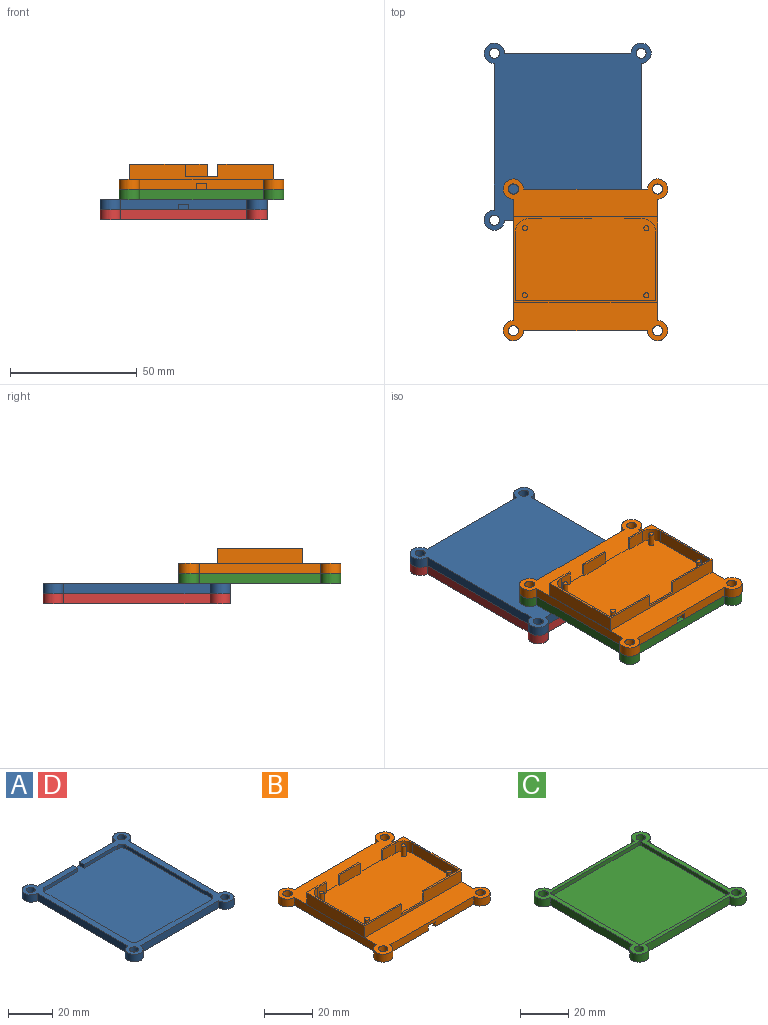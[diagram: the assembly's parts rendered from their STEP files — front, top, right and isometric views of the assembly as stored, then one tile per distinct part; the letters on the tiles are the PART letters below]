
ASSEMBLY  parts=4 mates=7
PART A: 26 faces, bbox 66x74x4 mm
  f0: plane 74x66mm, normal (0,0,1), area 804.3mm2, adj f1,f2,f3,f4,f5,f6,f7,f8
  f1: cylinder r=4mm len=8mm, axis (0,0,-1), area 75.4mm2, adj f0,f2,f8,f9
  f2: plane 50x4mm, normal (0,1,0), area 192mm2, adj f0,f1,f3,f9,f10,f11,f12
  f3: cylinder r=4mm len=8mm, axis (0,0,-1), area 75.4mm2, adj f0,f2,f4,f9
  f4: plane 58x4mm, normal (-1,0,0), area 232mm2, adj f0,f3,f5,f9
  f5: cylinder r=4mm len=8mm, axis (0,0,-1), area 75.4mm2, adj f0,f4,f6,f9
  f6: plane 50x4mm, normal (0,-1,0), area 200mm2, adj f0,f5,f7,f9
  f7: cylinder r=4mm len=8mm, axis (0,0,-1), area 75.4mm2, adj f0,f6,f8,f9
  f8: plane 58x4mm, normal (1,0,0), area 232mm2, adj f0,f1,f7,f9
  f9: plane 74x66mm, normal (0,0,-1), area 3928.5mm2, adj f1,f2,f3,f4,f5,f6,f7,f8
  f10: plane 3x2mm, normal (1,0,0), area 6mm2, adj f0,f2,f12,f15
  f11: plane 3x2mm, normal (-1,0,0), area 6mm2, adj f0,f2,f12,f13
  f12: plane 63x52mm, normal (0,0,1), area 3124.3mm2, adj f2,f10,f11,f13,f14,f15,f16,f17
  f13: plane 21x2mm, normal (0,-1,0), area 42mm2, adj f0,f11,f12,f22
  f14: plane 54x2mm, normal (-1,0,0), area 108mm2, adj f0,f12,f22,f25
  f15: plane 21x2mm, normal (0,-1,0), area 42mm2, adj f0,f10,f12,f23
  f16: plane 54x2mm, normal (1,0,0), area 108mm2, adj f0,f12,f23,f24
  f17: plane 46x2mm, normal (0,1,0), area 92mm2, adj f0,f12,f24,f25
  f18: cylinder r=2mm len=4mm, axis (0,0,-1), area 50.3mm2, adj f0,f9
  f19: cylinder r=2mm len=4mm, axis (0,0,-1), area 50.3mm2, adj f0,f9
  f20: cylinder r=2mm len=4mm, axis (0,0,-1), area 50.3mm2, adj f0,f9
  f21: cylinder r=2mm len=4mm, axis (0,0,-1), area 50.3mm2, adj f0,f9
  f22: cylinder r=3mm len=3mm, axis (0,0,1), area 9.4mm2, adj f0,f12,f13,f14
  f23: cylinder r=3mm len=3mm, axis (0,0,-1), area 9.4mm2, adj f0,f12,f15,f16
  f24: cylinder r=3mm len=3mm, axis (0,0,1), area 9.4mm2, adj f0,f12,f16,f17
  f25: cylinder r=3mm len=3mm, axis (0,0,-1), area 9.4mm2, adj f0,f12,f14,f17
PART B: 57 faces, bbox 65x64x10 mm
  f0: plane 65x64mm, normal (0,0,-1), area 478.4mm2, adj f27,f28,f29,f30,f31,f32,f33,f34
  f1: plane 33.9x22mm, normal (0,0,1), area 55.9mm2, adj f2,f7,f9,f10,f11,f13,f25,f36
  f2: plane 55.4x5.25mm, normal (0,1,0), area 226.3mm2, adj f1,f4,f12,f13,f14,f36,f37,f38
  f3: plane 12.25x0.75mm, normal (0,0,1), area 9.2mm2, adj f5,f7,f24,f26
  f4: plane 33.9x22mm, normal (0,0,1), area 54.4mm2, adj f2,f6,f7,f8,f9,f12,f23,f37
  f5: plane 12.25x5.25mm, normal (0,-1,0), area 64.3mm2, adj f3,f14,f24,f26
  f6: plane 5.25x5.2mm, normal (0,-1,0), area 27.3mm2, adj f4,f14,f23,f53
  f7: plane 56.9x6mm, normal (0,1,0), area 232.5mm2, adj f1,f3,f4,f8,f10,f14,f23,f24
  f8: plane 33.9x6mm, normal (-1,0,0), area 203.4mm2, adj f4,f7,f9,f35
  f9: plane 56.9x6mm, normal (0,-1,0), area 276.9mm2, adj f1,f4,f8,f10,f35,f36,f37,f38
  f10: plane 33.9x6mm, normal (1,0,0), area 203.4mm2, adj f1,f7,f9,f35
  f11: plane 7.2x5.25mm, normal (0,-1,0), area 37.8mm2, adj f1,f14,f25,f52
  f12: plane 27.4x5.25mm, normal (1,0,0), area 143.8mm2, adj f2,f4,f14,f53
  f13: plane 27.4x5.25mm, normal (-1,0,0), area 143.8mm2, adj f1,f2,f14,f52
  f14: plane 55.4x33.15mm, normal (0,0,1), area 1787.2mm2, adj f2,f5,f6,f7,f11,f12,f13,f15
  f15: cylinder r=1mm len=5.25mm, axis (0,0,-1), area 33mm2, adj f14,f16
  f16: plane 2x2mm, normal (0,0,1), area 3.1mm2, adj f15
  f17: cylinder r=1mm len=5.25mm, axis (0,0,-1), area 33mm2, adj f14,f18
  f18: plane 2x2mm, normal (0,0,1), area 3.1mm2, adj f17
  f19: cylinder r=1mm len=5.25mm, axis (0,0,-1), area 33mm2, adj f14,f20
  f20: plane 2x2mm, normal (0,0,1), area 3.1mm2, adj f19
  f21: cylinder r=1mm len=5.25mm, axis (0,0,-1), area 33mm2, adj f14,f22
  f22: plane 2x2mm, normal (0,0,1), area 3.1mm2, adj f21
  f23: plane 5.25x0.75mm, normal (1,0,0), area 3.9mm2, adj f4,f6,f7,f14
  f24: plane 5.25x0.75mm, normal (-1,0,0), area 3.9mm2, adj f3,f5,f7,f14
  f25: plane 5.25x0.75mm, normal (-1,0,0), area 3.9mm2, adj f1,f7,f11,f14
  f26: plane 5.25x0.75mm, normal (1,0,0), area 3.9mm2, adj f3,f5,f7,f14
  f27: cylinder r=4mm len=8mm, axis (0,0,1), area 75.4mm2, adj f0,f28,f34,f35
  f28: plane 49x4mm, normal (0,-1,0), area 186mm2, adj f0,f27,f29,f35,f54,f55,f56
  f29: cylinder r=4mm len=8mm, axis (0,0,1), area 75.4mm2, adj f0,f28,f30,f35
  f30: plane 48x4mm, normal (-1,0,0), area 192mm2, adj f0,f29,f31,f35
  f31: cylinder r=4mm len=8mm, axis (0,0,1), area 75.4mm2, adj f0,f30,f32,f35
  f32: plane 49x4mm, normal (0,1,0), area 196mm2, adj f0,f31,f33,f35
  f33: cylinder r=4mm len=8mm, axis (0,0,1), area 75.4mm2, adj f0,f32,f34,f35
  f34: plane 48x4mm, normal (1,0,0), area 192mm2, adj f0,f27,f33,f35
  f35: plane 65x64mm, normal (0,0,1), area 1363.6mm2, adj f7,f8,f9,f10,f27,f28,f29,f30
  f36: plane 5x0.75mm, normal (-1,0,0), area 3.8mm2, adj f1,f2,f9,f38
  f37: plane 5x0.75mm, normal (1,0,0), area 3.8mm2, adj f2,f4,f9,f38
  f38: plane 12.9x0.75mm, normal (0,0,1), area 9.7mm2, adj f2,f9,f36,f37
  f39: cylinder r=2mm len=4mm, axis (0,0,-1), area 50.3mm2, adj f0,f35
  f40: cylinder r=2mm len=4mm, axis (0,0,-1), area 50.3mm2, adj f0,f35
  f41: cylinder r=2mm len=4mm, axis (0,0,-1), area 50.3mm2, adj f0,f35
  f42: cylinder r=2mm len=4mm, axis (0,0,-1), area 50.3mm2, adj f0,f35
  f43: plane 51x3mm, normal (0,-1,0), area 153mm2, adj f0,f47,f48,f51
  f44: plane 51x3mm, normal (-1,0,0), area 153mm2, adj f0,f47,f48,f49
  f45: plane 51x3mm, normal (0,1,0), area 143mm2, adj f0,f47,f49,f50,f54,f55,f56
  f46: plane 51x3mm, normal (1,0,0), area 153mm2, adj f0,f47,f50,f51
  f47: plane 53x53mm, normal (0,0,-1), area 2808.1mm2, adj f43,f44,f45,f46,f48,f49,f50,f51
  f48: cylinder r=1mm len=3mm, axis (0,0,1), area 4.7mm2, adj f0,f43,f44,f47
  f49: cylinder r=1mm len=3mm, axis (0,0,-1), area 4.7mm2, adj f0,f44,f45,f47
  f50: cylinder r=1mm len=3mm, axis (0,0,1), area 4.7mm2, adj f0,f45,f46,f47
  f51: cylinder r=1mm len=3mm, axis (0,0,-1), area 4.7mm2, adj f0,f43,f46,f47
  f52: cylinder r=5mm len=5.25mm, axis (0,0,1), area 41.2mm2, adj f1,f11,f13,f14
  f53: cylinder r=5mm len=5.25mm, axis (0,0,-1), area 41.2mm2, adj f4,f6,f12,f14
  f54: plane 2.5x1.5mm, normal (-1,0,0), area 3.8mm2, adj f0,f28,f45,f55
  f55: plane 4x1.5mm, normal (0,0,-1), area 6mm2, adj f28,f45,f54,f56
  f56: plane 2.5x1.5mm, normal (1,0,0), area 3.8mm2, adj f0,f28,f45,f55
PART C: 23 faces, bbox 65x64x4 mm
  f0: plane 65x64mm, normal (0,0,1), area 484.4mm2, adj f1,f2,f3,f4,f5,f6,f7,f8
  f1: cylinder r=4mm len=8mm, axis (0,0,-1), area 75.4mm2, adj f0,f2,f8,f9
  f2: plane 49x4mm, normal (0,1,0), area 196mm2, adj f0,f1,f3,f9
  f3: cylinder r=4mm len=8mm, axis (0,0,-1), area 75.4mm2, adj f0,f2,f4,f9
  f4: plane 48x4mm, normal (-1,0,0), area 192mm2, adj f0,f3,f5,f9
  f5: cylinder r=4mm len=8mm, axis (0,0,-1), area 75.4mm2, adj f0,f4,f6,f9
  f6: plane 49x4mm, normal (0,-1,0), area 196mm2, adj f0,f5,f7,f9
  f7: cylinder r=4mm len=8mm, axis (0,0,-1), area 75.4mm2, adj f0,f6,f8,f9
  f8: plane 48x4mm, normal (1,0,0), area 192mm2, adj f0,f1,f7,f9
  f9: plane 65x64mm, normal (0,0,-1), area 3292.5mm2, adj f1,f2,f3,f4,f5,f6,f7,f8
  f10: cylinder r=2mm len=4mm, axis (0,0,1), area 50.3mm2, adj f0,f9
  f11: cylinder r=2mm len=4mm, axis (0,0,1), area 50.3mm2, adj f0,f9
  f12: cylinder r=2mm len=4mm, axis (0,0,1), area 50.3mm2, adj f0,f9
  f13: cylinder r=2mm len=4mm, axis (0,0,1), area 50.3mm2, adj f0,f9
  f14: plane 51x2mm, normal (0,1,0), area 102mm2, adj f0,f18,f19,f22
  f15: plane 51x2mm, normal (-1,0,0), area 102mm2, adj f0,f18,f19,f20
  f16: plane 51x2mm, normal (0,-1,0), area 102mm2, adj f0,f18,f20,f21
  f17: plane 51x2mm, normal (1,0,0), area 102mm2, adj f0,f18,f21,f22
  f18: plane 53x53mm, normal (0,0,1), area 2808.1mm2, adj f14,f15,f16,f17,f19,f20,f21,f22
  f19: cylinder r=1mm len=2mm, axis (0,0,-1), area 3.1mm2, adj f0,f14,f15,f18
  f20: cylinder r=1mm len=2mm, axis (0,0,1), area 3.1mm2, adj f0,f15,f16,f18
  f21: cylinder r=1mm len=2mm, axis (0,0,-1), area 3.1mm2, adj f0,f16,f17,f18
  f22: cylinder r=1mm len=2mm, axis (0,0,1), area 3.1mm2, adj f0,f14,f17,f18
PART D: same geometry as A
PLACE A rot(axis=(1,0,0),180deg) t=(-7.07,48.67,-8)mm
PLACE B at identity fixed
PLACE C rot(axis=(0,0,1),0deg) t=(0,0,-8)mm
PLACE D rot(axis=(0,0,1),0deg) t=(-7.07,48.67,-16)mm
MATE cylindrical C.f5 <-> B.f29  axis (0,0,-1) through (-28.5,-28,-8)mm
MATE cylindrical C.f1 <-> B.f33  axis (0,0,-1) through (28.5,28,-8)mm
MATE cylindrical D.f5 <-> A.f3  axis (0,0,-1) through (-36.07,15.67,-16)mm
MATE planar D.f0 <-> A.f0  axis (0,0,1) through (-7.07,48.2,-12)mm
MATE planar A.f9 <-> C.f9  axis (0,0,1) through (-7.07,48.67,-8)mm
MATE planar C.f0 <-> B.f0  axis (0,0,1) through (0,0,-4)mm
MATE cylindrical A.f7 <-> D.f1  axis (0,0,1) through (21.93,81.67,-10)mm
